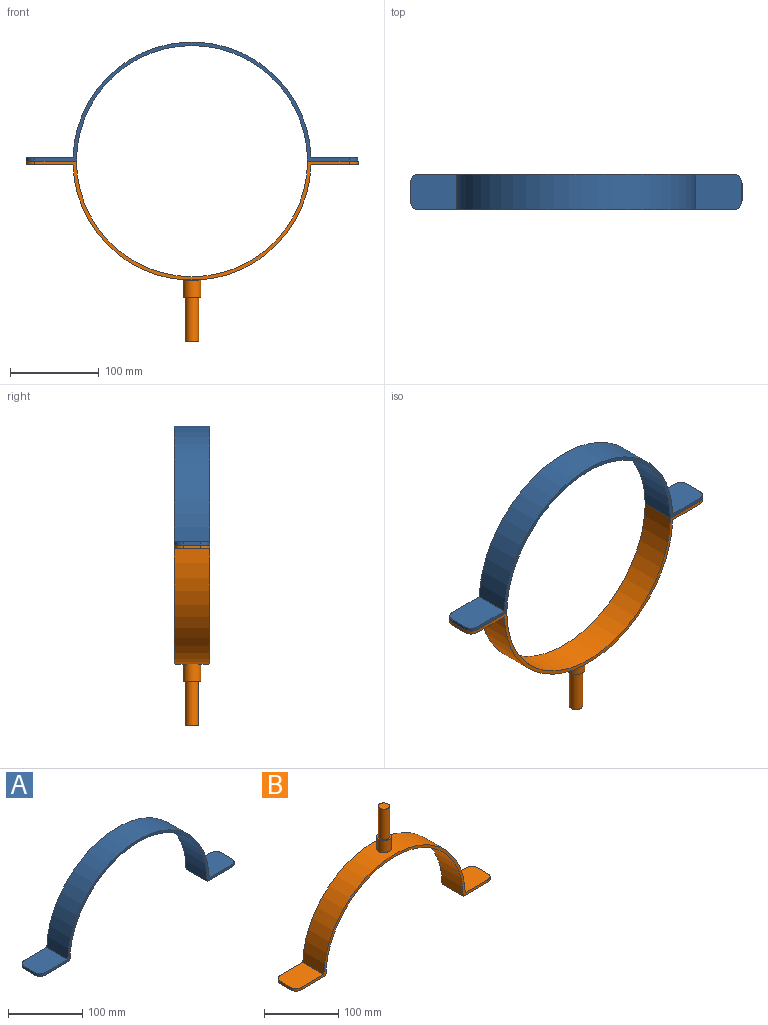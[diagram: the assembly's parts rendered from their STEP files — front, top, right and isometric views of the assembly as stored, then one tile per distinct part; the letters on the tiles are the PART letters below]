
ASSEMBLY  parts=2 mates=1
PART A: 14 faces, bbox 375x40x134.5 mm
  f0: plane 20x4mm, normal (1,0,0), area 80mm2, adj f1,f7,f11,f13
  f1: plane 53.06x40mm, normal (0,0,1), area 2079.5mm2, adj f0,f2,f8,f9,f11,f13
  f2: cylinder r=134.5mm len=268.88mm, axis (0,1,0), area 16581.7mm2, adj f1,f3,f8,f9
  f3: plane 53.06x40mm, normal (0,0,1), area 2079.5mm2, adj f2,f4,f8,f9,f10,f12
  f4: plane 20x4mm, normal (-1,0,0), area 80mm2, adj f3,f5,f10,f12
  f5: plane 57x40mm, normal (0,0,-1), area 2237.1mm2, adj f4,f6,f8,f9,f10,f12
  f6: cylinder r=130.5mm len=261mm, axis (0,1,0), area 16399.1mm2, adj f5,f7,f8,f9
  f7: plane 57x40mm, normal (0,0,-1), area 2237.1mm2, adj f0,f6,f8,f9,f11,f13
  f8: plane 355x134.5mm, normal (0,-1,0), area 2009.2mm2, adj f1,f2,f3,f5,f6,f7,f12,f13
  f9: plane 355x134.5mm, normal (0,1,0), area 2009.2mm2, adj f1,f2,f3,f5,f6,f7,f10,f11
  f10: cylinder r=10mm len=10mm, axis (0,0,-1), area 62.8mm2, adj f3,f4,f5,f9
  f11: cylinder r=10mm len=10mm, axis (0,0,1), area 62.8mm2, adj f0,f1,f7,f9
  f12: cylinder r=10mm len=10mm, axis (0,0,1), area 62.8mm2, adj f3,f4,f5,f8
  f13: cylinder r=10mm len=10mm, axis (0,0,-1), area 62.8mm2, adj f0,f1,f7,f8
PART B: 18 faces, bbox 375x40x204 mm
  f0: cylinder r=134.5mm len=268.88mm, axis (0,1,0), area 16268.1mm2, adj f2,f3,f8,f9,f14
  f1: plane 20x4mm, normal (1,0,0), area 80mm2, adj f2,f7,f11,f13
  f2: plane 53.06x40mm, normal (0,0,1), area 2079.5mm2, adj f0,f1,f8,f9,f11,f13
  f3: plane 53.06x40mm, normal (0,0,1), area 2079.5mm2, adj f0,f4,f8,f9,f10,f12
  f4: plane 20x4mm, normal (-1,0,0), area 80mm2, adj f3,f5,f10,f12
  f5: plane 57x40mm, normal (0,0,-1), area 2237.1mm2, adj f4,f6,f8,f9,f10,f12
  f6: cylinder r=130.5mm len=261mm, axis (0,1,0), area 16399.1mm2, adj f5,f7,f8,f9
  f7: plane 57x40mm, normal (0,0,-1), area 2237.1mm2, adj f1,f6,f8,f9,f11,f13
  f8: plane 355x134.5mm, normal (0,-1,0), area 2009.2mm2, adj f0,f2,f3,f5,f6,f7,f12,f13
  f9: plane 355x134.5mm, normal (0,1,0), area 2009.2mm2, adj f0,f2,f3,f5,f6,f7,f10,f11
  f10: cylinder r=10mm len=10mm, axis (0,0,-1), area 62.8mm2, adj f3,f4,f5,f9
  f11: cylinder r=10mm len=10mm, axis (0,0,1), area 62.8mm2, adj f1,f2,f7,f9
  f12: cylinder r=10mm len=10mm, axis (0,0,1), area 62.8mm2, adj f3,f4,f5,f8
  f13: cylinder r=10mm len=10mm, axis (0,0,-1), area 62.8mm2, adj f1,f2,f7,f8
  f14: cylinder r=10mm len=20mm, axis (0,0,-1), area 1236.9mm2, adj f0,f15
  f15: plane 20x20mm, normal (0,0,1), area 137.4mm2, adj f14,f16
  f16: cylinder r=7.5mm len=50mm, axis (0,0,-1), area 2356.2mm2, adj f15,f17
  f17: plane 15x15mm, normal (0,0,1), area 176.7mm2, adj f16
PLACE A t=(-114.97,-31.9,-43.54)mm
PLACE B rot(axis=(1,0,0),180deg) t=(-114.97,-71.9,-47.54)mm
MATE fastened B.f7 <-> A.f7  axis (0,0,1) through (43.53,-51.9,-45.54)mm
